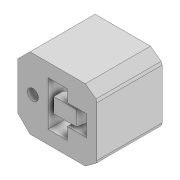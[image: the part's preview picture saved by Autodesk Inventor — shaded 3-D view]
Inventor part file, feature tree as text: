
AUTODESK INVENTOR PART (.ipt)
format: ipt  version: 2022 (Build 260153000, 153)  size: 464,384 bytes
history: native  units: in
note: dims shown in document units (in); Inventor stores cm internally (conversion verified against a paired STEP export)
features: projected_geometry x9, extrude x7, sketch x7, other x2, fillet x2, thicken_offset x2, plane x1, pattern_linear x1, chamfer x1
ambient origin geometry x8: Origin, YZ Plane, XZ Plane, XY Plane, X Axis, Y Axis, Z Axis, Center Point
bodies: Solid1 (feature_tree)
feature tree (32):
  other  "Cable_Tie1"
  other  "MeshFeature1"
  extrude  "Extrusion1"  Depth=0.0079in
  fillet  "Fillet1"  Radius=3.937in
  fillet  "Fillet2"  Radius=0.0984in
  plane  "Work Plane1"
  extrude  "Extrusion2"  Depth=0.063in
  extrude  "Extrusion4"  Depth=0.126in
  pattern_linear  "Rectangular Pattern1"  Spacing1=0.0984in  [1 undecoded]
  extrude  "Extrusion5"  Depth=0.4252in TaperAngle=0.0deg
  extrude  "Extrusion6"  Depth=0.0079in
  extrude  "Extrusion7"  Depth=0.0079in
  thicken_offset  "Thicken1"
  thicken_offset  "Thicken2"
  chamfer  "Chamfer1"  Distance=0.0394in
  extrude  "Extrusion8"  Depth=0.0079in
  sketch  "Sketch1"  dims[d0=0.0709in d1=0.0in d2=0.0079in d3=3.937in d4=0.0984in d5=0.0in]
  sketch  "Sketch2"  dims[d9=0.0197in d10=0.063in]
  projected_geometry  "Projected Loop1"
  sketch  "Sketch4"  dims[d11=0.1575in d12=0.0in d13=17.3228in d15=0.126in]
  projected_geometry  "Projected Loop2"
  projected_geometry  "Projected Loop3"
  sketch  "Sketch5"  dims[d16=0.3937in d17=0.0in]
  projected_geometry  "Projected Loop4"
  projected_geometry  "Projected Loop5"
  projected_geometry  "Projected Loop6"
  sketch  "Sketch6"  dims[d18=0.1969in]
  sketch  "Sketch7"  dims[d19=0.4252in d20=0.0in]
  sketch  "Sketch8"  dims[d21=0.0709in d22=0.0984in d23=0.4252in d24=0.0in d26=0.0394in d27=0.0394in d28=0.0394in d29=0.0394in d30=0.0787in d31=0.0787in d32=45.0deg d33=0.0079in d34=0.0in]
  projected_geometry  "Projected Loop7"
  projected_geometry  "Projected Loop8"
  projected_geometry  "Projected Loop9"
note: 1 required parameter value undecoded (feature->parameter linkage not recoverable at this tier; creation-order binding heuristic only, values carry confidence <= 0.55)
